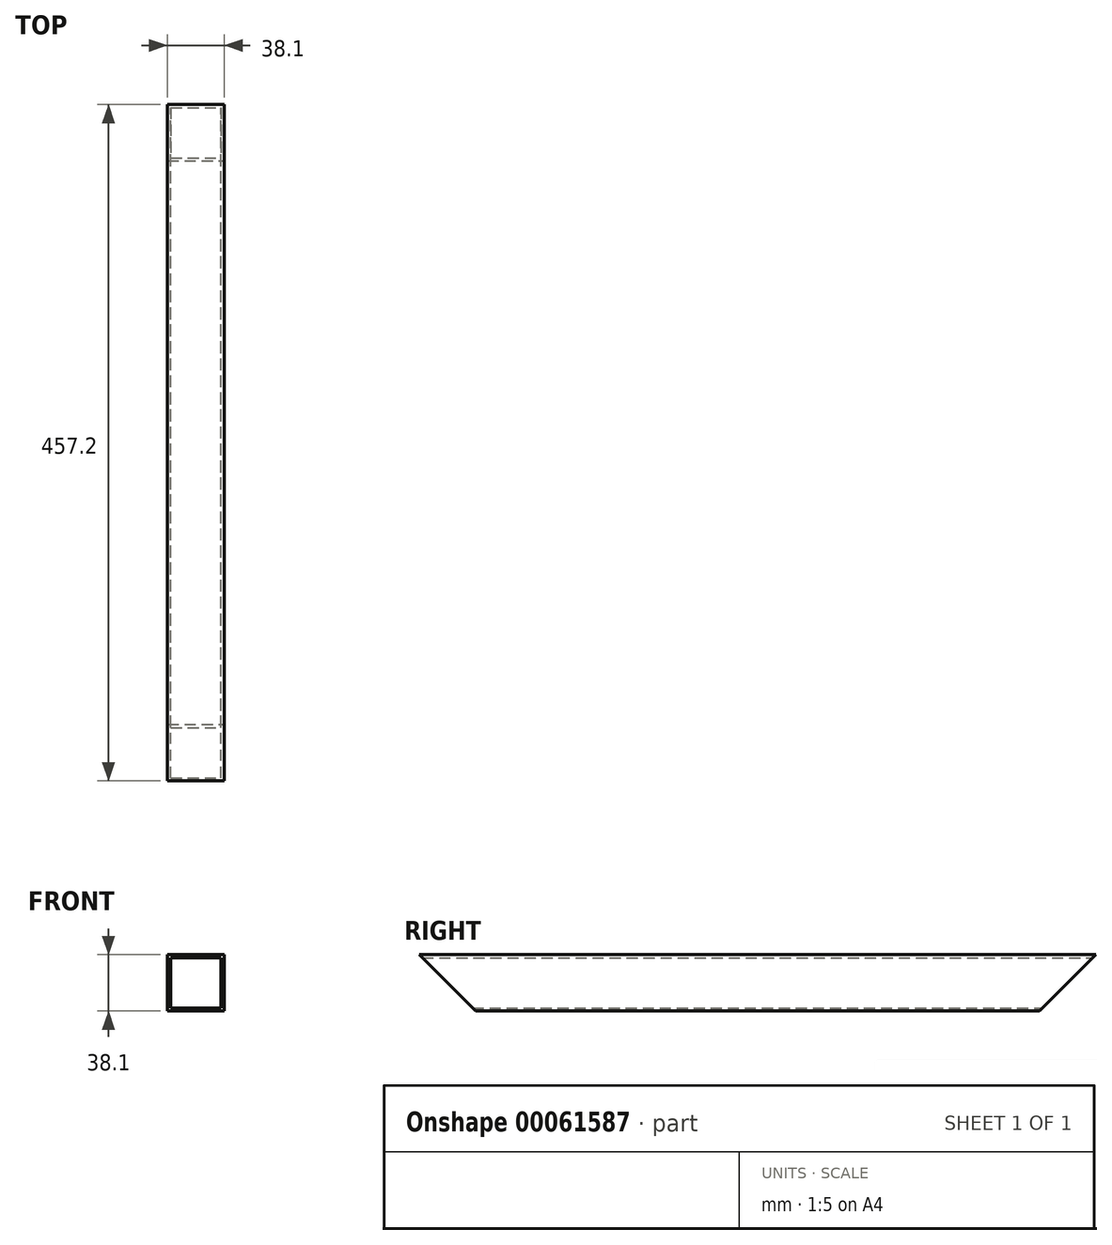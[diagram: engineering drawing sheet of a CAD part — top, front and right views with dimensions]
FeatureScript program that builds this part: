
annotation { "Feature Type Name" : "Feature", "Feature Type Description" : "" }
export const myFeature = defineFeature(function(context is Context, id is Id, definition is map)
    precondition{}
    {
        {
            var Q0;
            Q0=qCreatedBy(makeId("Front.planeOp"),FACE);
            var sketch = newSketch(context, id + "F0", { "sketchPlane" : qUnion([Q0])});
            skLineSegment(sketch, "E0.bottom", {"start": v(-19.05, 19.05) * mm, "end": v(19.05, 19.05) * mm});
            skLineSegment(sketch, "E0.top", {"start": v(-19.05, -19.05) * mm, "end": v(19.05, -19.05) * mm});
            skLineSegment(sketch, "E0.left", {"start": v(-19.05, 19.05) * mm, "end": v(-19.05, -19.05) * mm});
            skLineSegment(sketch, "E0.right", {"start": v(19.05, 19.05) * mm, "end": v(19.05, -19.05) * mm});
            skLineSegment(sketch, "E1.bottom", {"start": v(-16.94, 16.94) * mm, "end": v(16.94, 16.94) * mm});
            skLineSegment(sketch, "E1.top", {"start": v(-16.94, -16.94) * mm, "end": v(16.94, -16.94) * mm});
            skLineSegment(sketch, "E1.left", {"start": v(-16.94, 16.94) * mm, "end": v(-16.94, -16.94) * mm});
            skLineSegment(sketch, "E1.right", {"start": v(16.94, 16.94) * mm, "end": v(16.94, -16.94) * mm});
            skLineSegment(sketch, "E2", {"start": v(-19.05, 19.05) * mm, "end": v(19.05, -19.05) * mm, "construction": true});
            skSolve(sketch);
        }
        {
            var Q0;
            Q0=makeQuery(id+"F0.imprint","IMPRINT",FACE,{"disambiguationData":[TD([[makeQuery(id+"F0.imprint","IMPRINT",EDGE,{"derivedFrom":sQuery(id+"F0.wireOp",EDGE,"E0.bottom")}),-1.0]])]});
            extrude(context, id + "F1", {"entities" : qUnion([Q0]), "endBound" : BoundingType.SYMMETRIC, "depth" : 457.2 * mm});
        }
        {
            var Q0;
            Q0=makeQuery(id+"F1.opExtrude","SWEPT_FACE",FACE,{"disambiguationData":[OSD([sQuery(id+"F0.wireOp",EDGE,"E0.right")])]});
            var sketch = newSketch(context, id + "F2", { "sketchPlane" : qUnion([Q0])});
            skLineSegment(sketch, "E3", {"start": v(-228.6, 19.05) * mm, "end": v(-190.5, -19.05) * mm});
            skLineSegment(sketch, "E4", {"start": v(-190.5, -19.05) * mm, "end": v(-228.6, -19.05) * mm});
            skLineSegment(sketch, "E5", {"start": v(-228.6, -19.05) * mm, "end": v(-228.6, 19.05) * mm});
            skLineSegment(sketch, "E6.MirrorCS", {"start": v(228.6, 19.05) * mm, "end": v(190.5, -19.05) * mm});
            skLineSegment(sketch, "E7.MirrorCS", {"start": v(190.5, -19.05) * mm, "end": v(228.6, -19.05) * mm});
            skLineSegment(sketch, "E8.MirrorCS", {"start": v(228.6, -19.05) * mm, "end": v(228.6, 19.05) * mm});
            skSolve(sketch);
        }
        {
            var Q0;
            Q0=makeQuery(id+"F2.imprint","IMPRINT",FACE,{"disambiguationData":[TD([[makeQuery(id+"F2.imprint","IMPRINT",EDGE,{"derivedFrom":sQuery(id+"F2.wireOp",EDGE,"E3")}),-1.0]])]});
            var Q1;
            Q1=makeQuery(id+"F2.imprint","IMPRINT",FACE,{"disambiguationData":[TD([[makeQuery(id+"F2.imprint","IMPRINT",EDGE,{"derivedFrom":sQuery(id+"F2.wireOp",EDGE,"E6.MirrorCS")}),1.0]])]});
            extrude(context, id + "F3", {"entities" : qUnion([Q0, Q1]), "operationType" : NewBodyOperationType.REMOVE, "endBound" : BoundingType.THROUGH_ALL, "oppositeDirection" : true, "depth" : 25.4 * mm});
        }
    });
